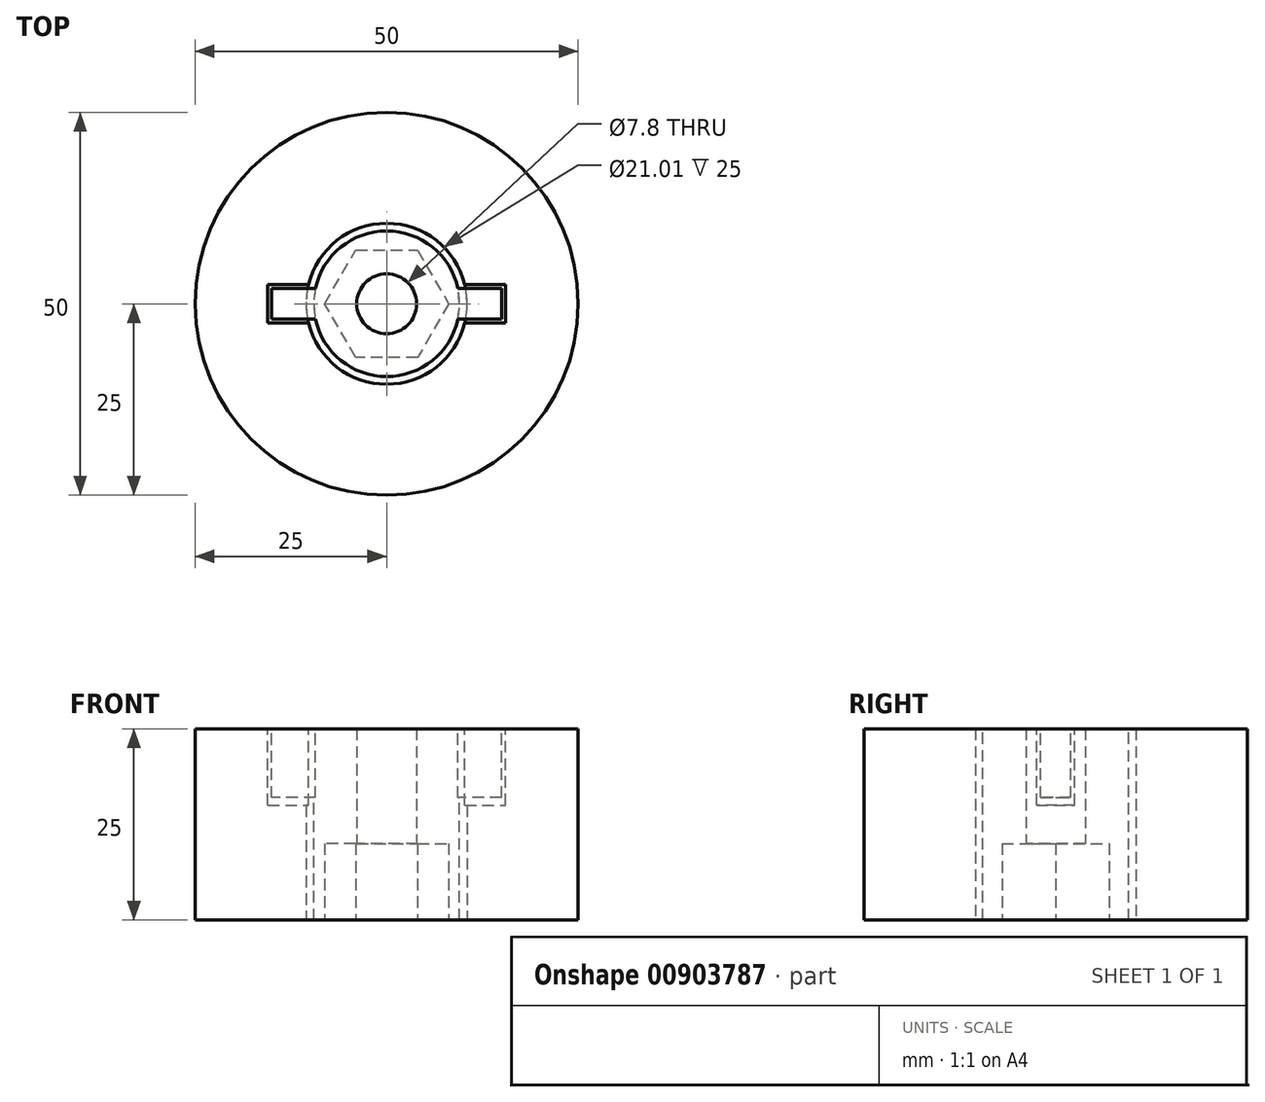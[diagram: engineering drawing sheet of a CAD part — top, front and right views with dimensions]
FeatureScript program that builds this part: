
annotation { "Feature Type Name" : "Feature", "Feature Type Description" : "" }
export const myFeature = defineFeature(function(context is Context, id is Id, definition is map)
    precondition{}
    {
        {
            var Q0;
            Q0=qCreatedBy(makeId("Top.planeOp"),FACE);
            var sketch = newSketch(context, id + "F0", { "sketchPlane" : qUnion([Q0])});
            skCircle(sketch, "E0", {"center": v(0, 0) * mm, "radius": 25 * mm});
            skCircle(sketch, "E1.cCircle", {"center": v(0, 0) * mm, "radius": 6.5 * mm, "construction": true});
            skLineSegment(sketch, "E1.0", {"start": v(-3.75, 6.5) * mm, "end": v(3.75, 6.5) * mm});
            skLineSegment(sketch, "E1.1", {"start": v(3.75, 6.5) * mm, "end": v(7.5, 0) * mm});
            skLineSegment(sketch, "E1.2", {"start": v(7.5, 0) * mm, "end": v(3.75, -6.5) * mm});
            skLineSegment(sketch, "E1.3", {"start": v(3.75, -6.5) * mm, "end": v(-3.75, -6.5) * mm});
            skLineSegment(sketch, "E1.4", {"start": v(-3.75, -6.5) * mm, "end": v(-7.5, 0) * mm});
            skLineSegment(sketch, "E1.5", {"start": v(-7.5, 0) * mm, "end": v(-3.75, 6.5) * mm});
            skPoint(sketch, "E1.0.midPoint", {"position": v(0, 6.5) * mm});
            skCircle(sketch, "E2", {"center": v(0, 0) * mm, "radius": 10.5 * mm});
            skSolve(sketch);
        }
        {
            var Q0;
            Q0=makeQuery(id+"F0.imprint","IMPRINT",FACE,{"disambiguationData":[TD([[makeQuery(id+"F0.imprint","IMPRINT",EDGE,{"derivedFrom":sQuery(id+"F0.wireOp",EDGE,"E0")}),1.0]])]});
            extrude(context, id + "F1", {"entities" : qUnion([Q0]), "depth" : 25 * mm, "offsetDistance" : 25 * mm});
        }
        {
            var Q0;
            Q0=makeQuery(id+"F0.imprint","IMPRINT",FACE,{"disambiguationData":[TD([[makeQuery(id+"F0.imprint","IMPRINT",EDGE,{"derivedFrom":sQuery(id+"F0.wireOp",EDGE,"E1.0")}),-1.0]])]});
            extrude(context, id + "F2", {"entities" : qUnion([Q0]), "depth" : 7 * mm, "offsetDistance" : 25 * mm});
        }
        {
            var Q0;
            Q0=sQuery(id+"F0.wireOp",VERTEX,"E0.center");
            var Q1;
            Q1=makeQuery(id+"F2.opExtrude","SWEPT_BODY",BODY,{"disambiguationData":[OSD([sQuery(id+"F0.wireOp",EDGE,"E1.0"),sQuery(id+"F0.wireOp",EDGE,"E1.1"),sQuery(id+"F0.wireOp",EDGE,"E1.2"),sQuery(id+"F0.wireOp",EDGE,"E1.3"),sQuery(id+"F0.wireOp",EDGE,"E1.4"),sQuery(id+"F0.wireOp",EDGE,"E1.5")])]});
            hole(context, id + "F3", {"style" : HoleStyle.SIMPLE, "endStyle" : HoleEndStyle.BLIND, "oppositeDirection" : true, "standardTappedOrClearance" : lookupTablePath({ "standard" : "ISO", "engagement" : "75%", "pitch" : "1.25 mm", "size" : "M8", "type" : "Tapped" }), "standardBlindInLast" : lookupTablePath({ "standard" : "ISO", "engagement" : "75%", "pitch" : "1.25 mm", "size" : "M8", "type" : "Tapped" }), "holeDiameter" : 6.8 * mm, "majorDiameter" : 8 * mm, "showTappedDepth" : true, "holeDepth" : 12.25 * mm, "isTappedThrough" : true, "tappedDepth" : 8.5 * mm, "tapClearance" : 3, "startFromSketch" : true, "locations" : qUnion([Q0]), "scope" : qUnion([Q1])});
        }
        {
            var Q0;
            Q0=makeQuery(id+"F1.opExtrude","CAP_FACE",FACE,{"disambiguationData":[OSD([sQuery(id+"F0.wireOp",EDGE,"E0"),sQuery(id+"F0.wireOp",EDGE,"E2")])],"isStart":false});
            var sketch = newSketch(context, id + "F4", { "sketchPlane" : qUnion([Q0])});
            skLineSegment(sketch, "E3.bottom", {"start": v(-15.5, 2.5) * mm, "end": v(15.5, 2.5) * mm});
            skLineSegment(sketch, "E3.top", {"start": v(-15.5, -2.5) * mm, "end": v(15.5, -2.5) * mm});
            skLineSegment(sketch, "E3.left", {"start": v(-15.5, 2.5) * mm, "end": v(-15.5, -2.5) * mm});
            skLineSegment(sketch, "E3.right", {"start": v(15.5, 2.5) * mm, "end": v(15.5, -2.5) * mm});
            skPoint(sketch, "E4", {"position": v(-15.5, 0) * mm});
            skPoint(sketch, "E5", {"position": v(0, 2.5) * mm});
            skSolve(sketch);
        }
        {
            var Q0;
            {var subQ0=sQuery(id+"F4.wireOp",EDGE,"E3.left");Q0=makeQuery(id+"F4.imprint","IMPRINT",FACE,{"disambiguationData":[TD([[makeQuery(id+"F4.imprint","IMPRINT",EDGE,{"derivedFrom":subQ0}),1.0]])]});}
            var Q1;
            {var subQ0=sQuery(id+"F4.wireOp",EDGE,"E3.right");Q1=makeQuery(id+"F4.imprint","IMPRINT",FACE,{"disambiguationData":[TD([[makeQuery(id+"F4.imprint","IMPRINT",EDGE,{"derivedFrom":subQ0}),-1.0]])]});}
            extrude(context, id + "F5", {"entities" : qUnion([Q0, Q1]), "operationType" : NewBodyOperationType.REMOVE, "oppositeDirection" : true, "depth" : 10 * mm, "offsetDistance" : 25 * mm});
        }
        {
            var Q0;
            Q0=makeQuery(id+"F1.opExtrude","CAP_FACE",FACE,{"disambiguationData":[OSD([sQuery(id+"F0.wireOp",EDGE,"E0"),sQuery(id+"F0.wireOp",EDGE,"E2")])],"isStart":false});
            var sketch = newSketch(context, id + "F6", { "sketchPlane" : qUnion([Q0])});
            skArc(sketch, "E6", {"start": v(-9.3, -2) * mm, "mid": v(0, -9.5) * mm, "end": v(9.3, -2) * mm});
            skLineSegment(sketch, "E7.bottom", {"start": v(-15, 2) * mm, "end": v(-9.3, 2) * mm});
            skLineSegment(sketch, "E7.top", {"start": v(-15, -2) * mm, "end": v(-9.3, -2) * mm});
            skLineSegment(sketch, "E7.left", {"start": v(-15, 2) * mm, "end": v(-15, -2) * mm});
            skLineSegment(sketch, "E7.right", {"start": v(15, 2) * mm, "end": v(15, -2) * mm});
            skLineSegment(sketch, "E8.trimOffspring", {"start": v(9.3, 2) * mm, "end": v(15, 2) * mm});
            skLineSegment(sketch, "E9.trimOffspring", {"start": v(9.3, -2) * mm, "end": v(15, -2) * mm});
            skArc(sketch, "E10.trimOffspring", {"start": v(9.3, 2) * mm, "mid": v(0, 9.5) * mm, "end": v(-9.3, 2) * mm});
            skSolve(sketch);
        }
        {
            var Q0;
            Q0=makeQuery(id+"F6.imprint","IMPRINT",FACE,{"disambiguationData":[TD([[makeQuery(id+"F6.imprint","IMPRINT",EDGE,{"derivedFrom":sQuery(id+"F6.wireOp",EDGE,"E6")}),1.0]])]});
            var Q1;
            Q1=makeQuery(id+"F5.boolean.opBoolean","COPY",FACE,{"derivedFrom":makeQuery(id+"F5.opExtrude","CAP_FACE",FACE,{"disambiguationData":[OSD([sQuery(id+"F0.wireOp",EDGE,"E2"),sQuery(id+"F4.wireOp",EDGE,"E3.bottom"),sQuery(id+"F4.wireOp",EDGE,"E3.top"),sQuery(id+"F4.wireOp",EDGE,"E3.right")])],"isStart":false})});
            extrude(context, id + "F7", {"entities" : qUnion([Q0]), "endBound" : BoundingType.UP_TO_SURFACE, "oppositeDirection" : true, "depth" : 25 * mm, "endBoundEntityFace" : qUnion([Q1]), "hasOffset" : true, "offsetDistance" : 1 * mm});
        }
        {
            var Q0;
            Q0=makeQuery(id+"F7.opExtrude","CAP_FACE",FACE,{"disambiguationData":[OSD([sQuery(id+"F6.wireOp",EDGE,"E6"),sQuery(id+"F6.wireOp",EDGE,"E7.bottom"),sQuery(id+"F6.wireOp",EDGE,"E7.top"),sQuery(id+"F6.wireOp",EDGE,"E7.left"),sQuery(id+"F6.wireOp",EDGE,"E7.right"),sQuery(id+"F6.wireOp",EDGE,"E8.trimOffspring"),sQuery(id+"F6.wireOp",EDGE,"E9.trimOffspring"),sQuery(id+"F6.wireOp",EDGE,"E10.trimOffspring")])],"isStart":false});
            var sketch = newSketch(context, id + "F8", { "sketchPlane" : qUnion([Q0])});
            skCircle(sketch, "E11", {"center": v(0, 0) * mm, "radius": 9.5 * mm});
            skSolve(sketch);
        }
        {
            var Q0;
            {var subQ0=sQuery(id+"F8.wireOp",EDGE,"E11");var subQ1=makeQuery(id+"F8.imprint","INTERSECT",VERTEX,{"derivedFrom":[makeQuery(id+"F7.opExtrude","CAP_EDGE",EDGE,{"disambiguationData":[OSD([sQuery(id+"F6.wireOp",EDGE,"E7.bottom")])],"isStart":false}),subQ0]});Q0=makeQuery(id+"F8.imprint","IMPRINT",FACE,{"disambiguationData":[TD([[makeQuery(id+"F8.imprint","IMPRINT",EDGE,{"disambiguationData":[TD([[subQ1,-1.0]])],"derivedFrom":subQ0}),1.0]])]});}
            var Q1;
            Q1=makeQuery(id+"F1.opExtrude","CAP_FACE",FACE,{"disambiguationData":[OSD([sQuery(id+"F0.wireOp",EDGE,"E0"),sQuery(id+"F0.wireOp",EDGE,"E2")])],"isStart":true});
            extrude(context, id + "F9", {"entities" : qUnion([Q0]), "operationType" : NewBodyOperationType.ADD, "endBound" : BoundingType.UP_TO_SURFACE, "depth" : 25 * mm, "endBoundEntityFace" : qUnion([Q1]), "offsetDistance" : 25 * mm});
        }
        {
            var Q0;
            Q0=makeQuery(id+"F9.opExtrude","CAP_FACE",FACE,{"disambiguationData":[OSD([sQuery(id+"F8.wireOp",EDGE,"E11")])],"isStart":false});
            var sketch = newSketch(context, id + "F10", { "sketchPlane" : qUnion([Q0])});
            skLineSegment(sketch, "E12.0", {"start": v(-3.75, 6.5) * mm, "end": v(-7.5, 0) * mm});
            skLineSegment(sketch, "E12.1", {"start": v(3.75, 6.5) * mm, "end": v(-3.75, 6.5) * mm});
            skLineSegment(sketch, "E12.2", {"start": v(7.5, 0) * mm, "end": v(3.75, 6.5) * mm});
            skLineSegment(sketch, "E12.3", {"start": v(3.75, -6.5) * mm, "end": v(7.5, 0) * mm});
            skLineSegment(sketch, "E12.4", {"start": v(-3.75, -6.5) * mm, "end": v(3.75, -6.5) * mm});
            skLineSegment(sketch, "E12.5", {"start": v(-7.5, 0) * mm, "end": v(-3.75, -6.5) * mm});
            skLineSegment(sketch, "E13.0", {"start": v(4.04, 7) * mm, "end": v(-4.04, 7) * mm});
            skLineSegment(sketch, "E13.1", {"start": v(-8.08, 0) * mm, "end": v(-4.04, -7) * mm});
            skLineSegment(sketch, "E13.2", {"start": v(-4.04, -7) * mm, "end": v(4.04, -7) * mm});
            skLineSegment(sketch, "E13.3", {"start": v(-4.04, 7) * mm, "end": v(-8.08, 0) * mm});
            skLineSegment(sketch, "E13.4", {"start": v(4.04, -7) * mm, "end": v(8.08, 0) * mm});
            skLineSegment(sketch, "E13.5", {"start": v(8.08, 0) * mm, "end": v(4.04, 7) * mm});
            skCircle(sketch, "E14.0", {"center": v(0, 0) * mm, "radius": 3.9 * mm});
            skSolve(sketch);
        }
        {
            var Q0;
            Q0=makeQuery(id+"F10.imprint","IMPRINT",FACE,{"disambiguationData":[TD([[makeQuery(id+"F10.imprint","IMPRINT",EDGE,{"derivedFrom":sQuery(id+"F10.wireOp",EDGE,"E12.0")}),-1.0]])]});
            var Q1;
            Q1=makeQuery(id+"F10.imprint","IMPRINT",FACE,{"disambiguationData":[TD([[makeQuery(id+"F10.imprint","IMPRINT",EDGE,{"derivedFrom":sQuery(id+"F10.wireOp",EDGE,"E12.0")}),1.0]])]});
            var Q2;
            Q2=makeQuery(id+"F10.imprint","IMPRINT",FACE,{"disambiguationData":[TD([[makeQuery(id+"F10.imprint","IMPRINT",EDGE,{"derivedFrom":sQuery(id+"F10.wireOp",EDGE,"E14.0")}),1.0]])]});
            extrude(context, id + "F11", {"entities" : qUnion([Q0, Q1, Q2]), "operationType" : NewBodyOperationType.REMOVE, "oppositeDirection" : true, "depth" : 10 * mm, "offsetDistance" : 25 * mm});
        }
        {
            var Q0;
            Q0=makeQuery(id+"F10.imprint","IMPRINT",FACE,{"disambiguationData":[TD([[makeQuery(id+"F10.imprint","IMPRINT",EDGE,{"derivedFrom":sQuery(id+"F10.wireOp",EDGE,"E14.0")}),1.0]])]});
            var Q1;
            Q1=makeQuery(id+"F7.opExtrude","CAP_FACE",FACE,{"disambiguationData":[OSD([sQuery(id+"F6.wireOp",EDGE,"E6"),sQuery(id+"F6.wireOp",EDGE,"E7.bottom"),sQuery(id+"F6.wireOp",EDGE,"E7.top"),sQuery(id+"F6.wireOp",EDGE,"E7.left"),sQuery(id+"F6.wireOp",EDGE,"E7.right"),sQuery(id+"F6.wireOp",EDGE,"E8.trimOffspring"),sQuery(id+"F6.wireOp",EDGE,"E9.trimOffspring"),sQuery(id+"F6.wireOp",EDGE,"E10.trimOffspring")])],"isStart":true});
            extrude(context, id + "F12", {"entities" : qUnion([Q0]), "operationType" : NewBodyOperationType.REMOVE, "endBound" : BoundingType.UP_TO_SURFACE, "oppositeDirection" : true, "depth" : 25 * mm, "endBoundEntityFace" : qUnion([Q1]), "offsetDistance" : 25 * mm});
        }
    });
